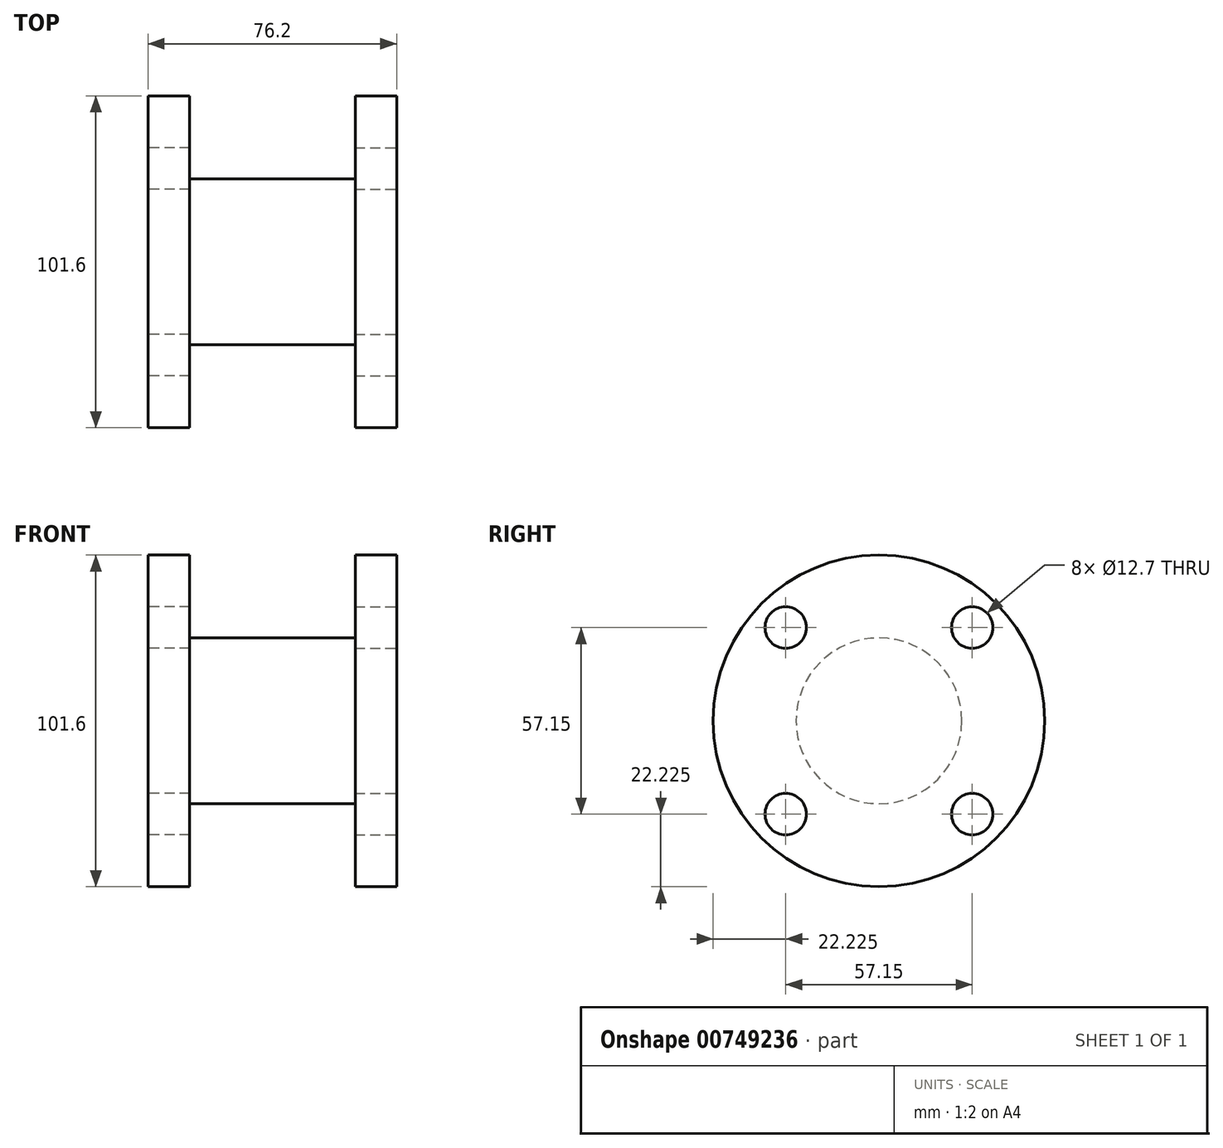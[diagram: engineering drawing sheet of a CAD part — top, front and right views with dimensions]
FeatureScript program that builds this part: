
annotation { "Feature Type Name" : "Feature", "Feature Type Description" : "" }
export const myFeature = defineFeature(function(context is Context, id is Id, definition is map)
    precondition{}
    {
        {
            var Q0;
            Q0=qCreatedBy(makeId("Right.planeOp"),FACE);
            var sketch = newSketch(context, id + "F0", { "sketchPlane" : qUnion([Q0])});
            skCircle(sketch, "E0", {"center": v(0, 0) * mm, "radius": 50.8 * mm});
            skCircle(sketch, "E1", {"center": v(0, 0) * mm, "radius": 19.05 * mm});
            skLineSegment(sketch, "E2", {"start": v(0, 0) * mm, "end": v(76.99, 0) * mm});
            skLineSegment(sketch, "E3", {"start": v(0, 0) * mm, "end": v(-65.76, 0) * mm, "construction": true});
            skLineSegment(sketch, "E4", {"start": v(0, 50.8) * mm, "end": v(0, -54.83) * mm, "construction": true});
            skCircle(sketch, "E5", {"center": v(-28.57, 28.58) * mm, "radius": 6.35 * mm});
            skCircle(sketch, "E6", {"center": v(28.58, 28.58) * mm, "radius": 6.35 * mm});
            skCircle(sketch, "E7", {"center": v(28.58, -28.58) * mm, "radius": 6.35 * mm});
            skCircle(sketch, "E8", {"center": v(-28.57, -28.58) * mm, "radius": 6.35 * mm});
            skSolve(sketch);
        }
        {
            var Q0;
            Q0=makeQuery(id+"F0.imprint","IMPRINT",FACE,{"disambiguationData":[TD([[makeQuery(id+"F0.imprint","IMPRINT",EDGE,{"derivedFrom":sQuery(id+"F0.wireOp",EDGE,"E0")}),1.0]])]});
            extrude(context, id + "F1", {"entities" : qUnion([Q0]), "depth" : 12.7 * mm, "offsetDistance" : 25.4 * mm});
        }
        {
            var Q0;
            Q0=qCreatedBy(makeId("Right.planeOp"),FACE);
            var sketch = newSketch(context, id + "F2", { "sketchPlane" : qUnion([Q0])});
            skCircle(sketch, "E9", {"center": v(0, 0) * mm, "radius": 25.4 * mm});
            skSolve(sketch);
        }
        {
            var Q0;
            Q0 = qSketchRegion(id + "F2", true);
            extrude(context, id + "F3", {"entities" : qUnion([Q0]), "operationType" : NewBodyOperationType.ADD, "depth" : 38.1 * mm, "offsetDistance" : 25.4 * mm});
        }
        {
            var Q0;
            Q0=makeQuery(id+"F1.opExtrude","SWEPT_BODY",BODY,{"disambiguationData":[OSD([sQuery(id+"F0.wireOp",EDGE,"E0"),sQuery(id+"F0.wireOp",EDGE,"E1"),sQuery(id+"F0.wireOp",EDGE,"E5"),sQuery(id+"F0.wireOp",EDGE,"E6"),sQuery(id+"F0.wireOp",EDGE,"E7"),sQuery(id+"F0.wireOp",EDGE,"E8")])]});
            var Q1;
            Q1=makeQuery(id+"F3.opExtrude","CAP_FACE",FACE,{"disambiguationData":[OSD([sQuery(id+"F2.wireOp",EDGE,"E9")])],"isStart":false});
            mirror(context, id + "F4", {"operationType" : NewBodyOperationType.ADD, "entities" : qUnion([Q0]), "mirrorPlane" : qUnion([Q1])});
        }
    });
